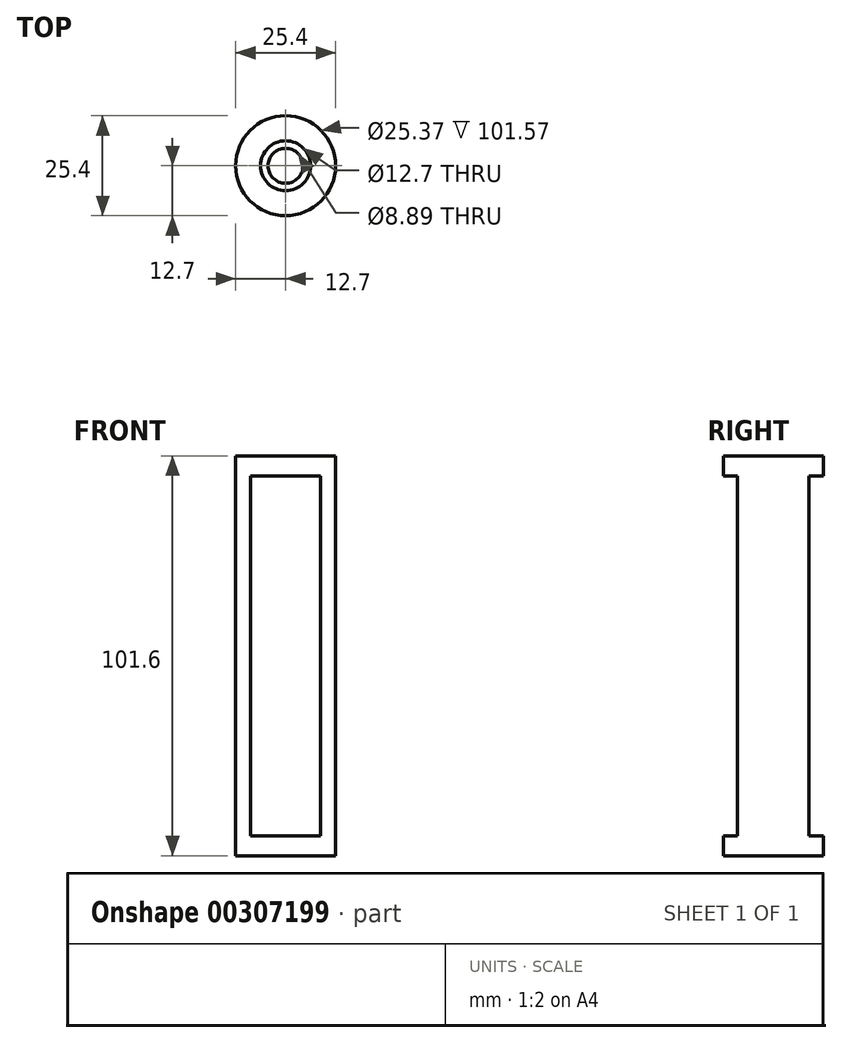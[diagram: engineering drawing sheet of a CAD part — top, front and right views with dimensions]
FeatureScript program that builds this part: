
annotation { "Feature Type Name" : "Feature", "Feature Type Description" : "" }
export const myFeature = defineFeature(function(context is Context, id is Id, definition is map)
    precondition{}
    {
        {
            var Q0;
            Q0=qCreatedBy(makeId("Top.planeOp"),FACE);
            var sketch = newSketch(context, id + "F0", { "sketchPlane" : qUnion([Q0])});
            skCircle(sketch, "E0", {"center": v(0, 0) * mm, "radius": 12.7 * mm});
            skSolve(sketch);
        }
        {
            var Q0;
            Q0 = qSketchRegion(id + "F0", true);
            extrude(context, id + "F1", {"entities" : qUnion([Q0]), "depth" : 101.6 * mm});
        }
        {
            var Q0;
            Q0=makeQuery(id+"F1.opExtrude","SWEPT_FACE",FACE,{"disambiguationData":[OSD([sQuery(id+"F0.wireOp",EDGE,"E0")])]});
            var Q1;
            Q1=makeQuery(id+"F1.opExtrude","SWEPT_BODY",BODY,{"disambiguationData":[OSD([sQuery(id+"F0.wireOp",EDGE,"E0")])]});
            shell(context, id + "F2", {"isHollow" : true, "entities" : qUnion([Q0]), "parts" : qUnion([Q1]), "thickness" : 3 / 203.2 * mm});
        }
        {
            var Q0;
            Q0=qCreatedBy(makeId("Front.planeOp"),FACE);
            var sketch = newSketch(context, id + "F3", { "sketchPlane" : qUnion([Q0])});
            skLineSegment(sketch, "E1", {"start": v(0, 0) * mm, "end": v(0, 101.6) * mm});
            skLineSegment(sketch, "E2.bottom", {"start": v(8.9, 5.08) * mm, "end": v(-8.9, 5.08) * mm});
            skLineSegment(sketch, "E2.top", {"start": v(8.9, 96.52) * mm, "end": v(-8.9, 96.52) * mm});
            skLineSegment(sketch, "E2.left", {"start": v(8.9, 5.08) * mm, "end": v(8.9, 96.52) * mm});
            skLineSegment(sketch, "E2.right", {"start": v(-8.9, 5.08) * mm, "end": v(-8.9, 96.52) * mm});
            skPoint(sketch, "E2.middle", {"position": v(0, 50.8) * mm});
            skLineSegment(sketch, "E3", {"start": v(-20.86, 101.6) * mm, "end": v(22.18, 101.6) * mm});
            skLineSegment(sketch, "E4", {"start": v(-21.04, 0) * mm, "end": v(21.8, 0) * mm});
            skSolve(sketch);
        }
        {
            var Q0;
            Q0 = qSketchRegion(id + "F3", true);
            extrude(context, id + "F4", {"entities" : qUnion([Q0]), "operationType" : NewBodyOperationType.REMOVE, "endBound" : BoundingType.THROUGH_ALL, "oppositeDirection" : true, "depth" : 53.02 * mm, "hasSecondDirection" : true, "secondDirectionOppositeDirection" : false, "secondDirectionDepth" : 25.4 * mm});
        }
        {
            var Q0;
            Q0=makeQuery(id+"F1.opExtrude","CAP_FACE",FACE,{"disambiguationData":[OSD([sQuery(id+"F0.wireOp",EDGE,"E0")])],"isStart":false});
            var sketch = newSketch(context, id + "F5", { "sketchPlane" : qUnion([Q0])});
            skCircle(sketch, "E5", {"center": v(0, 0) * mm, "radius": 6.35 * mm});
            skSolve(sketch);
        }
        {
            var Q0;
            Q0 = qSketchRegion(id + "F5", true);
            extrude(context, id + "F6", {"entities" : qUnion([Q0]), "operationType" : NewBodyOperationType.REMOVE, "oppositeDirection" : true, "depth" : 25.4 * mm});
        }
        {
            var Q0;
            Q0=makeQuery(id+"F4.boolean.opBoolean","COPY",FACE,{"derivedFrom":makeQuery(id+"F4.opExtrude","SWEPT_FACE",FACE,{"disambiguationData":[OSD([sQuery(id+"F3.wireOp",EDGE,"E2.bottom")])]})});
            var sketch = newSketch(context, id + "F7", { "sketchPlane" : qUnion([Q0])});
            skCircle(sketch, "E6", {"center": v(0, 0) * mm, "radius": 12.7 * mm});
            skCircle(sketch, "E7", {"center": v(0, 0) * mm, "radius": 4.45 * mm});
            skSolve(sketch);
        }
        {
            var Q0;
            Q0=makeQuery(id+"F7.imprint","IMPRINT",FACE,{"disambiguationData":[TD([[makeQuery(id+"F7.imprint","IMPRINT",EDGE,{"derivedFrom":sQuery(id+"F7.wireOp",EDGE,"E7")}),1.0]])]});
            extrude(context, id + "F8", {"entities" : qUnion([Q0]), "operationType" : NewBodyOperationType.REMOVE, "oppositeDirection" : true, "depth" : 25.4 * mm});
        }
    });
